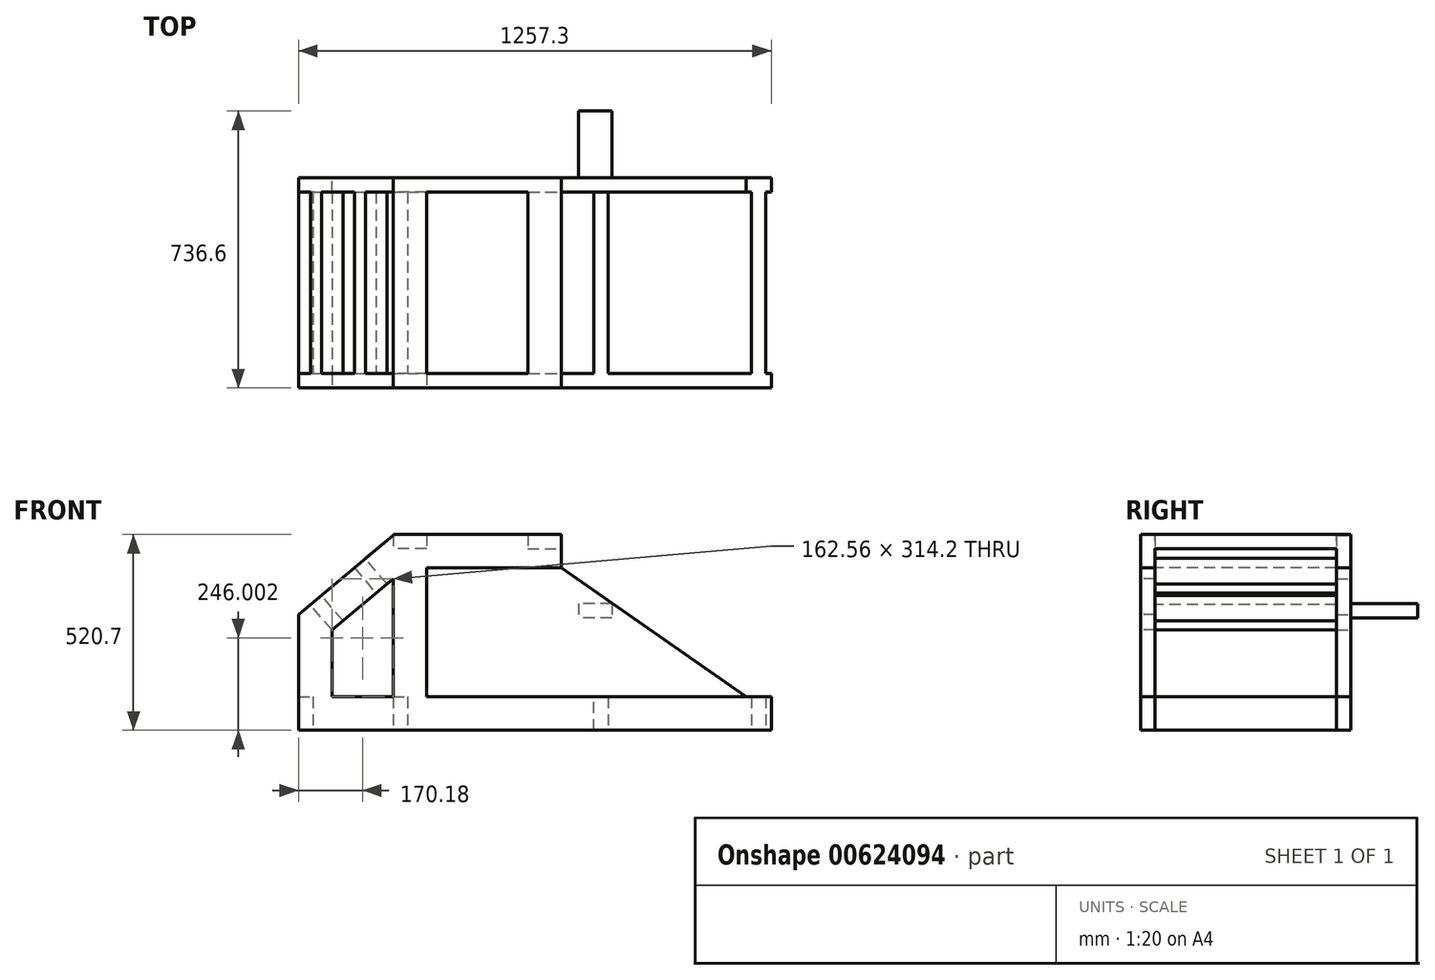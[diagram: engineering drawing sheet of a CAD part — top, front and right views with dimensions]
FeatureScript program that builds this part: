
annotation { "Feature Type Name" : "Feature", "Feature Type Description" : "" }
export const myFeature = defineFeature(function(context is Context, id is Id, definition is map)
    precondition{}
    {
        {
            var Q0;
            Q0=qCreatedBy(makeId("Front.planeOp"),FACE);
            var sketch = newSketch(context, id + "F0", { "sketchPlane" : qUnion([Q0])});
            skLineSegment(sketch, "E0", {"start": v(0, 0) * mm, "end": v(1257.3, 0) * mm});
            skLineSegment(sketch, "E1", {"start": v(0, 0) * mm, "end": v(0, 88.9) * mm});
            skLineSegment(sketch, "E2", {"start": v(1257.3, 0) * mm, "end": v(1257.3, 88.9) * mm});
            skLineSegment(sketch, "E3", {"start": v(1257.3, 88.9) * mm, "end": v(0, 88.9) * mm});
            skLineSegment(sketch, "E4", {"start": v(251.46, 88.9) * mm, "end": v(251.46, 520.7) * mm});
            skLineSegment(sketch, "E5", {"start": v(0, 88.9) * mm, "end": v(0, 308.15) * mm});
            skLineSegment(sketch, "E6", {"start": v(0, 308.15) * mm, "end": v(251.46, 519.15) * mm});
            skLineSegment(sketch, "E7.0", {"start": v(88.9, 266.7) * mm, "end": v(251.46, 403.1) * mm});
            skLineSegment(sketch, "E8.0", {"start": v(88.9, 25.4) * mm, "end": v(88.9, 266.7) * mm});
            skLineSegment(sketch, "E9.0", {"start": v(340.36, 25.4) * mm, "end": v(340.36, 520.7) * mm});
            skLineSegment(sketch, "E10", {"start": v(251.46, 520.7) * mm, "end": v(340.36, 520.7) * mm});
            skLineSegment(sketch, "E11", {"start": v(340.36, 520.7) * mm, "end": v(698.5, 520.7) * mm});
            skLineSegment(sketch, "E12", {"start": v(698.5, 520.7) * mm, "end": v(698.5, 431.8) * mm});
            skLineSegment(sketch, "E13", {"start": v(698.5, 431.8) * mm, "end": v(340.36, 431.8) * mm});
            skLineSegment(sketch, "E14", {"start": v(698.5, 431.8) * mm, "end": v(673.1, 431.8) * mm});
            skLineSegment(sketch, "E15", {"start": v(698.5, 431.8) * mm, "end": v(452.3, 88.9) * mm});
            skLineSegment(sketch, "E16.0", {"start": v(589.06, 431.8) * mm, "end": v(342.86, 88.9) * mm});
            skLineSegment(sketch, "E17", {"start": v(762, 88.9) * mm, "end": v(762, 0) * mm, "construction": true});
            skSolve(sketch);
        }
        {
            var Q0;
            {var subQ6=sQuery(id+"F0.wireOp",EDGE,"E9.0");Q0=makeQuery(id+"F0.imprint","IMPRINT",FACE,{"disambiguationData":[TD([[makeQuery(id+"F0.imprint","IMPRINT",EDGE,{"derivedFrom":subQ6}),1.0]])]});}
            var Q1;
            {var subQ0=sQuery(id+"F0.wireOp",EDGE,"E5");Q1=makeQuery(id+"F0.imprint","IMPRINT",FACE,{"disambiguationData":[TD([[makeQuery(id+"F0.imprint","IMPRINT",EDGE,{"derivedFrom":subQ0}),-1.0]])]});}
            var Q2;
            Q2=makeQuery(id+"F0.imprint","IMPRINT",FACE,{"disambiguationData":[TD([[makeQuery(id+"F0.imprint","IMPRINT",EDGE,{"derivedFrom":sQuery(id+"F0.wireOp",EDGE,"E0")}),1.0]])]});
            var Q3;
            {var subQ3=sQuery(id+"F0.wireOp",EDGE,"E11");Q3=makeQuery(id+"F0.imprint","IMPRINT",FACE,{"disambiguationData":[TD([[makeQuery(id+"F0.imprint","IMPRINT",EDGE,{"derivedFrom":subQ3}),-1.0]])]});}
            var Q4;
            {var subQ0=sQuery(id+"F0.wireOp",EDGE,"RTkG8WMZ-2bth-Vol4-fops-xo588kz0touc");Q4=makeQuery(id+"F0.imprint","IMPRINT",FACE,{"disambiguationData":[TD([[makeQuery(id+"F0.imprint","IMPRINT",EDGE,{"derivedFrom":subQ0}),-1.0]])]});}
            var Q5;
            {var subQ0=sQuery(id+"F0.wireOp",EDGE,"E14");Q5=makeQuery(id+"F0.imprint","IMPRINT",FACE,{"disambiguationData":[TD([[makeQuery(id+"F0.imprint","IMPRINT",EDGE,{"derivedFrom":subQ0}),1.0]])]});}
            extrude(context, id + "F1", {"entities" : qUnion([Q0, Q1, Q2, Q3, Q4, Q5]), "oppositeDirection" : true, "depth" : 38.1 * mm, "offsetDistance" : 25.4 * mm});
        }
        {
            var Q0;
            Q0=makeQuery(id+"F1.opExtrude","CAP_FACE",FACE,{"disambiguationData":[OSD([sQuery(id+"F0.wireOp",EDGE,"E0"),sQuery(id+"F0.wireOp",EDGE,"E1"),sQuery(id+"F0.wireOp",EDGE,"E2"),sQuery(id+"F0.wireOp",EDGE,"E3"),sQuery(id+"F0.wireOp",EDGE,"E4"),sQuery(id+"F0.wireOp",EDGE,"E5"),sQuery(id+"F0.wireOp",EDGE,"E6"),sQuery(id+"F0.wireOp",EDGE,"E7.0"),sQuery(id+"F0.wireOp",EDGE,"E8.0"),sQuery(id+"F0.wireOp",EDGE,"E9.0"),sQuery(id+"F0.wireOp",EDGE,"E10"),sQuery(id+"F0.wireOp",EDGE,"E11"),sQuery(id+"F0.wireOp",EDGE,"E12"),sQuery(id+"F0.wireOp",EDGE,"E13"),sQuery(id+"F0.wireOp",EDGE,"E15"),sQuery(id+"F0.wireOp",EDGE,"E16.0")])],"isStart":false});
            cPlane(context, id + "F2", {"entities" : qUnion([Q0]), "cplaneType" : CPlaneType.OFFSET, "offset" : 241.3 * mm, "width" : 152.4 * mm, "height" : 152.4 * mm});
        }
        {
            var Q0;
            Q0=makeQuery(id+"F1.opExtrude","SWEPT_BODY",BODY,{"disambiguationData":[OSD([sQuery(id+"F0.wireOp",EDGE,"E0"),sQuery(id+"F0.wireOp",EDGE,"E1"),sQuery(id+"F0.wireOp",EDGE,"E2"),sQuery(id+"F0.wireOp",EDGE,"E3"),sQuery(id+"F0.wireOp",EDGE,"E4"),sQuery(id+"F0.wireOp",EDGE,"E5"),sQuery(id+"F0.wireOp",EDGE,"E6"),sQuery(id+"F0.wireOp",EDGE,"E7.0"),sQuery(id+"F0.wireOp",EDGE,"E8.0"),sQuery(id+"F0.wireOp",EDGE,"E9.0"),sQuery(id+"F0.wireOp",EDGE,"E10"),sQuery(id+"F0.wireOp",EDGE,"E11"),sQuery(id+"F0.wireOp",EDGE,"E12"),sQuery(id+"F0.wireOp",EDGE,"E13"),sQuery(id+"F0.wireOp",EDGE,"E15"),sQuery(id+"F0.wireOp",EDGE,"E16.0")])]});
            var Q1;
            Q1=qCreatedBy(id+"F2.planeOp",FACE);
            mirror(context, id + "F3", {"entities" : qUnion([Q0]), "mirrorPlane" : qUnion([Q1])});
        }
        {
            var Q0;
            Q0=makeQuery(id+"F1.opExtrude","CAP_FACE",FACE,{"disambiguationData":[OSD([sQuery(id+"F0.wireOp",EDGE,"E0"),sQuery(id+"F0.wireOp",EDGE,"E1"),sQuery(id+"F0.wireOp",EDGE,"E2"),sQuery(id+"F0.wireOp",EDGE,"E3"),sQuery(id+"F0.wireOp",EDGE,"E4"),sQuery(id+"F0.wireOp",EDGE,"E5"),sQuery(id+"F0.wireOp",EDGE,"E6"),sQuery(id+"F0.wireOp",EDGE,"E7.0"),sQuery(id+"F0.wireOp",EDGE,"E8.0"),sQuery(id+"F0.wireOp",EDGE,"E9.0"),sQuery(id+"F0.wireOp",EDGE,"E10"),sQuery(id+"F0.wireOp",EDGE,"E11"),sQuery(id+"F0.wireOp",EDGE,"E12"),sQuery(id+"F0.wireOp",EDGE,"E13"),sQuery(id+"F0.wireOp",EDGE,"E15"),sQuery(id+"F0.wireOp",EDGE,"E16.0")])],"isStart":false});
            var sketch = newSketch(context, id + "F4", { "sketchPlane" : qUnion([Q0])});
            skLineSegment(sketch, "E18.bottom", {"start": v(0, 0) * mm, "end": v(-88.9, 0) * mm});
            skLineSegment(sketch, "E18.top", {"start": v(0, 88.9) * mm, "end": v(-88.9, 88.9) * mm});
            skLineSegment(sketch, "E18.left", {"start": v(0, 0) * mm, "end": v(0, 88.9) * mm});
            skLineSegment(sketch, "E19.bottom", {"start": v(-251.46, 88.9) * mm, "end": v(-289.56, 88.9) * mm});
            skLineSegment(sketch, "E19.top", {"start": v(-251.46, 0) * mm, "end": v(-289.56, 0) * mm});
            skLineSegment(sketch, "E19.left", {"start": v(-251.46, 88.9) * mm, "end": v(-251.46, 0) * mm});
            skLineSegment(sketch, "E19.right", {"start": v(-289.56, 88.9) * mm, "end": v(-289.56, 0) * mm});
            skLineSegment(sketch, "E20.bottom", {"start": v(-251.46, 520.7) * mm, "end": v(-340.36, 520.7) * mm});
            skLineSegment(sketch, "E20.left", {"start": v(-251.46, 520.7) * mm, "end": v(-251.46, 431.8) * mm});
            skLineSegment(sketch, "E20.right", {"start": v(-340.36, 520.7) * mm, "end": v(-340.36, 431.8) * mm});
            skLineSegment(sketch, "E21.bottom", {"start": v(-698.5, 520.7) * mm, "end": v(-609.6, 520.7) * mm});
            skLineSegment(sketch, "E21.left", {"start": v(-698.5, 520.7) * mm, "end": v(-698.5, 431.8) * mm});
            skLineSegment(sketch, "E21.right", {"start": v(-609.6, 520.7) * mm, "end": v(-609.6, 431.8) * mm});
            skLineSegment(sketch, "E22.bottom", {"start": v(-698.5, 88.9) * mm, "end": v(-822.96, 88.9) * mm});
            skLineSegment(sketch, "E22.top", {"start": v(-698.5, 0) * mm, "end": v(-822.96, 0) * mm});
            skLineSegment(sketch, "E22.right", {"start": v(-822.96, 88.9) * mm, "end": v(-822.96, 0) * mm});
            skLineSegment(sketch, "E23.bottom", {"start": v(-1203.96, 88.9) * mm, "end": v(-1242.06, 88.9) * mm});
            skLineSegment(sketch, "E23.top", {"start": v(-1203.96, 0) * mm, "end": v(-1242.06, 0) * mm});
            skLineSegment(sketch, "E23.left", {"start": v(-1203.96, 88.9) * mm, "end": v(-1203.96, 0) * mm});
            skLineSegment(sketch, "E23.right", {"start": v(-1242.06, 88.9) * mm, "end": v(-1242.06, 0) * mm});
            skLineSegment(sketch, "E24", {"start": v(-88.9, 266.7) * mm, "end": v(-31.76, 334.8) * mm});
            skLineSegment(sketch, "E25", {"start": v(-118.09, 291.2) * mm, "end": v(-60.94, 359.3) * mm});
            skLineSegment(sketch, "E26", {"start": v(-234.83, 389.15) * mm, "end": v(-177.69, 457.25) * mm});
            skLineSegment(sketch, "E27", {"start": v(-177.69, 457.25) * mm, "end": v(-148.5, 432.76) * mm});
            skLineSegment(sketch, "E28", {"start": v(-148.5, 432.76) * mm, "end": v(-205.65, 364.66) * mm});
            skLineSegment(sketch, "E29", {"start": v(-38.1, 88.9) * mm, "end": v(-38.1, 0) * mm});
            skLineSegment(sketch, "E30", {"start": v(-784.86, 0) * mm, "end": v(-784.86, 88.9) * mm});
            skLineSegment(sketch, "E31", {"start": v(-609.6, 482.6) * mm, "end": v(-698.5, 482.6) * mm});
            skLineSegment(sketch, "E32", {"start": v(-340.36, 482.6) * mm, "end": v(-251.46, 482.6) * mm});
            skSolve(sketch);
        }
        {
            var Q0;
            {var subQ1=sQuery(id+"F4.wireOp",EDGE,"E20.bottom");Q0=makeQuery(id+"F4.imprint","IMPRINT",FACE,{"disambiguationData":[TD([[makeQuery(id+"F4.imprint","IMPRINT",EDGE,{"derivedFrom":subQ1}),1.0]])]});}
            var Q1;
            Q1=makeQuery(id+"F4.imprint","IMPRINT",FACE,{"disambiguationData":[TD([[makeQuery(id+"F4.imprint","IMPRINT",EDGE,{"derivedFrom":sQuery(id+"F4.wireOp",EDGE,"E21.bottom")}),1.0]])]});
            var Q2;
            {var subQ0=sQuery(id+"F4.wireOp",EDGE,"E24");Q2=makeQuery(id+"F4.imprint","IMPRINT",FACE,{"disambiguationData":[TD([[makeQuery(id+"F4.imprint","IMPRINT",EDGE,{"derivedFrom":subQ0}),1.0]])]});}
            var Q3;
            Q3=makeQuery(id+"F4.imprint","IMPRINT",FACE,{"disambiguationData":[TD([[makeQuery(id+"F4.imprint","IMPRINT",EDGE,{"derivedFrom":sQuery(id+"F4.wireOp",EDGE,"E18.bottom")}),-1.0]])]});
            var Q4;
            Q4=makeQuery(id+"F4.imprint","IMPRINT",FACE,{"disambiguationData":[TD([[makeQuery(id+"F4.imprint","IMPRINT",EDGE,{"derivedFrom":sQuery(id+"F4.wireOp",EDGE,"E19.top")}),-1.0]])]});
            var Q5;
            Q5=makeQuery(id+"F4.imprint","IMPRINT",FACE,{"disambiguationData":[TD([[makeQuery(id+"F4.imprint","IMPRINT",EDGE,{"derivedFrom":sQuery(id+"F4.wireOp",EDGE,"E22.bottom")}),-1.0]])]});
            var Q6;
            Q6=makeQuery(id+"F4.imprint","IMPRINT",FACE,{"disambiguationData":[TD([[makeQuery(id+"F4.imprint","IMPRINT",EDGE,{"derivedFrom":sQuery(id+"F4.wireOp",EDGE,"E23.bottom")}),-1.0]])]});
            var Q7;
            {var subQ0=sQuery(id+"F4.wireOp",EDGE,"E26");Q7=makeQuery(id+"F4.imprint","IMPRINT",FACE,{"disambiguationData":[TD([[makeQuery(id+"F4.imprint","IMPRINT",EDGE,{"derivedFrom":subQ0}),-1.0]])]});}
            var Q8;
            Q8=makeQuery(id+"F3.opPattern","COPY",FACE,{"derivedFrom":makeQuery(id+"F1.opExtrude","CAP_FACE",FACE,{"disambiguationData":[OSD([sQuery(id+"F0.wireOp",EDGE,"E0"),sQuery(id+"F0.wireOp",EDGE,"E1"),sQuery(id+"F0.wireOp",EDGE,"E2"),sQuery(id+"F0.wireOp",EDGE,"E3"),sQuery(id+"F0.wireOp",EDGE,"E4"),sQuery(id+"F0.wireOp",EDGE,"E5"),sQuery(id+"F0.wireOp",EDGE,"E6"),sQuery(id+"F0.wireOp",EDGE,"E7.0"),sQuery(id+"F0.wireOp",EDGE,"E8.0"),sQuery(id+"F0.wireOp",EDGE,"E9.0"),sQuery(id+"F0.wireOp",EDGE,"E10"),sQuery(id+"F0.wireOp",EDGE,"E11"),sQuery(id+"F0.wireOp",EDGE,"E12"),sQuery(id+"F0.wireOp",EDGE,"E13"),sQuery(id+"F0.wireOp",EDGE,"E15"),sQuery(id+"F0.wireOp",EDGE,"E16.0")])],"isStart":false}),"instanceName":"1"});
            extrude(context, id + "F5", {"entities" : qUnion([Q0, Q1, Q2, Q3, Q4, Q5, Q6, Q7]), "operationType" : NewBodyOperationType.ADD, "endBound" : BoundingType.UP_TO_SURFACE, "depth" : 25.4 * mm, "endBoundEntityFace" : qUnion([Q8]), "offsetDistance" : 25.4 * mm});
        }
        {
            var Q0;
            Q0=makeQuery(id+"F3.opPattern","COPY",FACE,{"derivedFrom":makeQuery(id+"F1.opExtrude","CAP_FACE",FACE,{"disambiguationData":[OSD([sQuery(id+"F0.wireOp",EDGE,"E0"),sQuery(id+"F0.wireOp",EDGE,"E1"),sQuery(id+"F0.wireOp",EDGE,"E2"),sQuery(id+"F0.wireOp",EDGE,"E3"),sQuery(id+"F0.wireOp",EDGE,"E4"),sQuery(id+"F0.wireOp",EDGE,"E5"),sQuery(id+"F0.wireOp",EDGE,"E6"),sQuery(id+"F0.wireOp",EDGE,"E7.0"),sQuery(id+"F0.wireOp",EDGE,"E8.0"),sQuery(id+"F0.wireOp",EDGE,"E9.0"),sQuery(id+"F0.wireOp",EDGE,"E10"),sQuery(id+"F0.wireOp",EDGE,"E11"),sQuery(id+"F0.wireOp",EDGE,"E12"),sQuery(id+"F0.wireOp",EDGE,"E13"),sQuery(id+"F0.wireOp",EDGE,"E15"),sQuery(id+"F0.wireOp",EDGE,"E16.0")])],"isStart":true}),"instanceName":"1"});
            var sketch = newSketch(context, id + "F6", { "sketchPlane" : qUnion([Q0])});
            skLineSegment(sketch, "E33", {"start": v(-698.5, 431.8) * mm, "end": v(-1190.28, 88.9) * mm});
            skLineSegment(sketch, "E34", {"start": v(-1034.85, 88.9) * mm, "end": v(-646.65, 359.58) * mm});
            skSolve(sketch);
        }
        {
            var Q0;
            {var subQ0=sQuery(id+"F6.wireOp",EDGE,"E33");Q0=makeQuery(id+"F6.imprint","IMPRINT",FACE,{"disambiguationData":[TD([[makeQuery(id+"F6.imprint","IMPRINT",EDGE,{"derivedFrom":subQ0}),1.0]])]});}
            extrude(context, id + "F7", {"entities" : qUnion([Q0]), "operationType" : NewBodyOperationType.ADD, "oppositeDirection" : true, "depth" : 38.1 * mm, "offsetDistance" : 25.4 * mm});
        }
        {
            var Q0;
            {var subQ0=sQuery(id+"F0.wireOp",EDGE,"E15");var subQ1=sQuery(id+"F0.wireOp",EDGE,"E3");Q0=makeQuery(id+"F7.boolean.opBoolean","MERGE",FACE,{"derivedFrom":[makeQuery(id+"F3.opPattern","COPY",FACE,{"derivedFrom":makeQuery(id+"F1.opExtrude","CAP_FACE",FACE,{"disambiguationData":[OSD([sQuery(id+"F0.wireOp",EDGE,"E0"),sQuery(id+"F0.wireOp",EDGE,"E1"),sQuery(id+"F0.wireOp",EDGE,"E2"),subQ1,sQuery(id+"F0.wireOp",EDGE,"E4"),sQuery(id+"F0.wireOp",EDGE,"E5"),sQuery(id+"F0.wireOp",EDGE,"E6"),sQuery(id+"F0.wireOp",EDGE,"E7.0"),sQuery(id+"F0.wireOp",EDGE,"E8.0"),sQuery(id+"F0.wireOp",EDGE,"E9.0"),sQuery(id+"F0.wireOp",EDGE,"E10"),sQuery(id+"F0.wireOp",EDGE,"E11"),sQuery(id+"F0.wireOp",EDGE,"E12"),sQuery(id+"F0.wireOp",EDGE,"E13"),subQ0,sQuery(id+"F0.wireOp",EDGE,"E16.0")])],"isStart":true}),"instanceName":"1"}),makeQuery(id+"F7.opExtrude","CAP_FACE",FACE,{"disambiguationData":[OSD([subQ1,subQ0,sQuery(id+"F6.wireOp",EDGE,"E33"),sQuery(id+"F6.wireOp",EDGE,"E34")])],"isStart":true})]});}
            var sketch = newSketch(context, id + "F8", { "sketchPlane" : qUnion([Q0])});
            skLineSegment(sketch, "E35.bottom", {"start": v(-833.72, 337.52) * mm, "end": v(-744.82, 337.52) * mm});
            skLineSegment(sketch, "E35.top", {"start": v(-833.72, 299.42) * mm, "end": v(-744.82, 299.42) * mm});
            skLineSegment(sketch, "E35.left", {"start": v(-833.72, 337.52) * mm, "end": v(-833.72, 299.42) * mm});
            skLineSegment(sketch, "E35.right", {"start": v(-744.82, 337.52) * mm, "end": v(-744.82, 299.42) * mm});
            skSolve(sketch);
        }
        {
            var Q0;
            Q0=makeQuery(id+"F8.imprint","IMPRINT",FACE,{"disambiguationData":[TD([[makeQuery(id+"F8.imprint","IMPRINT",EDGE,{"derivedFrom":sQuery(id+"F8.wireOp",EDGE,"E35.bottom")}),-1.0]])]});
            extrude(context, id + "F9", {"entities" : qUnion([Q0]), "operationType" : NewBodyOperationType.ADD, "depth" : 177.8 * mm, "offsetDistance" : 25.4 * mm});
        }
    });
